# Revit family: Awning - 4X LT (AUS) FACADE AWNING WIN
name_source: partatom
category: Windows
units: mm (PartAtom-declared; Revit-internal decimal feet)

## family parameters
Always vertical = Yes
Cut with Voids When Loaded = No
Host = Wall
Room Calculation Point = No
Shared = No

## types (1)
- 4890 (W) X 2800 (H)
    Analytic Construction = 1/8 in Pilkington single glazing
    Construction Type Id = GSP4R
    Default Head Height = 2950 mm  [stored 9.67848 ft]
    Define Thermal Properties by = Schematic Type
    Description = Awning Window
    Heat Transfer Coefficient (U) = 3.6886 W/(m²·K)
    Height = 2800 mm  [stored 9.18635 ft]
    Operation = UserDefined
    Rough Height = 2860 mm  [stored 9.3832 ft]
    Rough Width = 4900 mm  [stored 16.0761 ft]
    Solar Heat Gain Coefficient = 0.78
    Thermal Resistance (R) = 0.2711 (m²·K)/W
    Visual Light Transmittance = 0.9
    Width = 4850 mm

note: [stored X ft] marks values corroborated as IEEE doubles in the binary element streams (Revit-internal decimal feet)

## geometry (parser evidence)
native form markers: Sweep x4
no freeform markers — native parametric forms only
